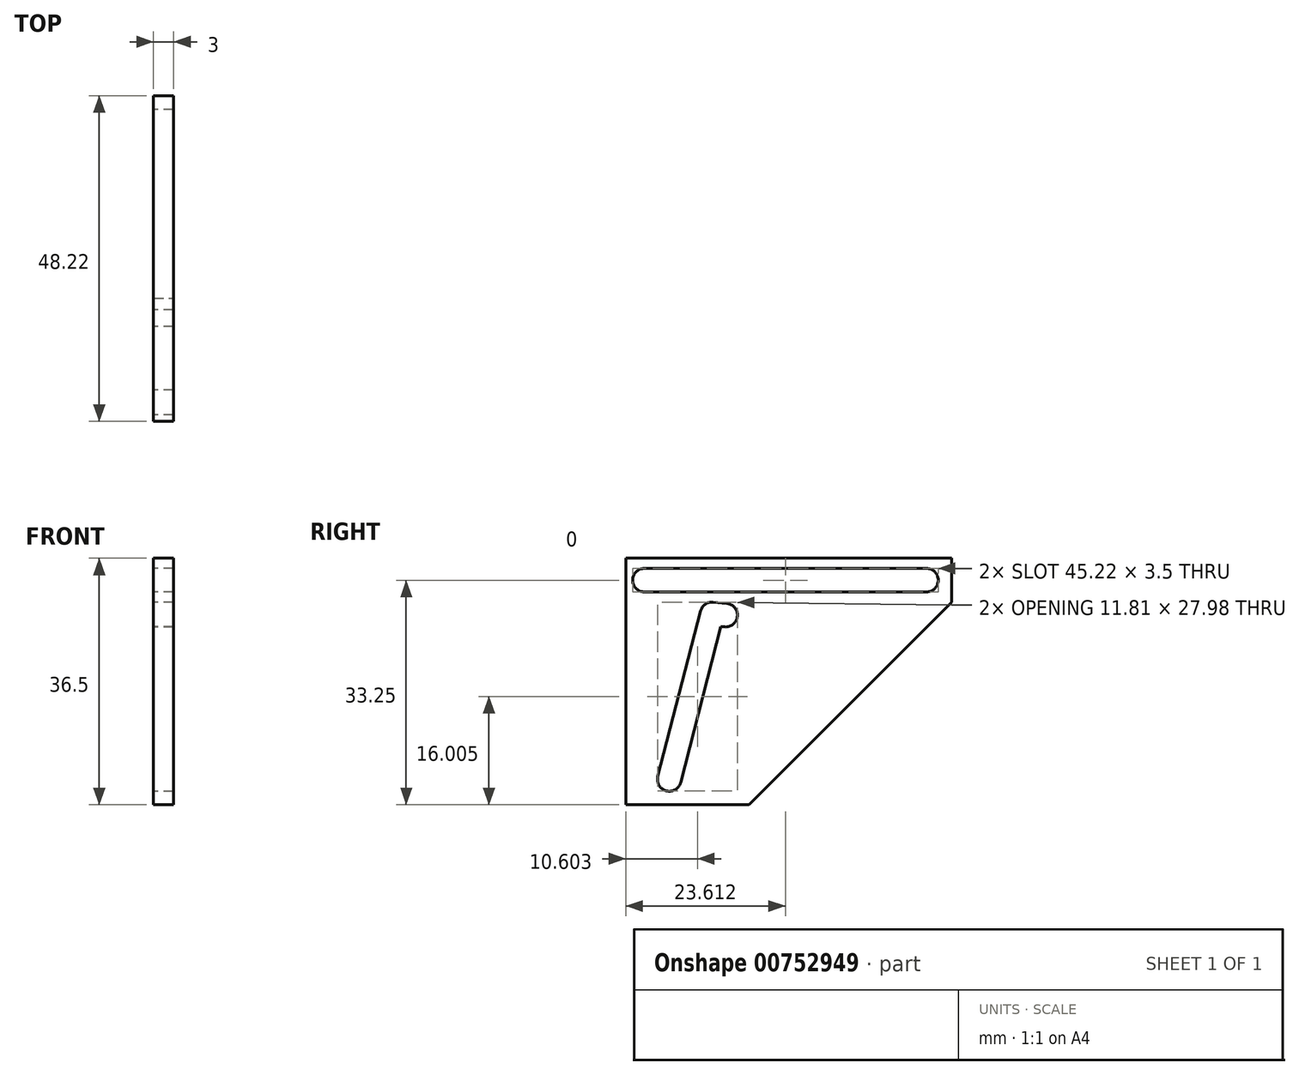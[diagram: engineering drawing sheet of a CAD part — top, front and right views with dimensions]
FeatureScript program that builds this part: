
annotation { "Feature Type Name" : "Feature", "Feature Type Description" : "" }
export const myFeature = defineFeature(function(context is Context, id is Id, definition is map)
    precondition{}
    {
        {
            var Q0;
            Q0=qCreatedBy(makeId("Right.planeOp"),FACE);
            var sketch = newSketch(context, id + "F0", { "sketchPlane" : qUnion([Q0])});
            skLineSegment(sketch, "E0", {"start": v(0, 29.5) * mm, "end": v(41.72, 29.5) * mm});
            skLineSegment(sketch, "E1", {"start": v(3.68, 0) * mm, "end": v(10, 24.5) * mm});
            skLineSegment(sketch, "E2.bottom", {"start": v(-2.75, 32.75) * mm, "end": v(45.47, 32.75) * mm});
            skLineSegment(sketch, "E2.top", {"start": v(-2.75, -3.75) * mm, "end": v(45.47, -3.75) * mm});
            skLineSegment(sketch, "E2.left", {"start": v(-2.75, 32.75) * mm, "end": v(-2.75, -3.75) * mm});
            skLineSegment(sketch, "E2.right", {"start": v(45.47, 32.75) * mm, "end": v(45.47, -3.75) * mm});
            skArc(sketch, "E3.0.startCap", {"start": v(0, 27.75) * mm, "mid": v(-1.75, 29.5) * mm, "end": v(0, 31.25) * mm});
            skArc(sketch, "E3.0.endCap", {"start": v(41.72, 31.25) * mm, "mid": v(43.47, 29.5) * mm, "end": v(41.72, 27.75) * mm});
            skLineSegment(sketch, "E3.0.left", {"start": v(0, 31.25) * mm, "end": v(41.72, 31.25) * mm});
            skLineSegment(sketch, "E3.0.right", {"start": v(0, 27.75) * mm, "end": v(41.72, 27.75) * mm});
            skArc(sketch, "E3.1.startCap", {"start": v(5.38, -0.44) * mm, "mid": v(3.24, -1.7) * mm, "end": v(1.99, 0.44) * mm});
            skArc(sketch, "E3.1.endCap", {"start": v(8.3, 24.94) * mm, "mid": v(10.44, 26.2) * mm, "end": v(11.7, 24.06) * mm});
            skLineSegment(sketch, "E3.1.left", {"start": v(1.99, 0.44) * mm, "end": v(8.3, 24.94) * mm});
            skLineSegment(sketch, "E3.1.right", {"start": v(5.38, -0.44) * mm, "end": v(11.7, 24.06) * mm});
            skLineSegment(sketch, "E4", {"start": v(10, 24.5) * mm, "end": v(12.01, 24.32) * mm});
            skArc(sketch, "E5.0.startCap", {"start": v(9.85, 22.76) * mm, "mid": v(8.26, 24.65) * mm, "end": v(10.15, 26.24) * mm});
            skArc(sketch, "E5.0.endCap", {"start": v(12.17, 26.07) * mm, "mid": v(13.76, 24.17) * mm, "end": v(11.86, 22.58) * mm});
            skLineSegment(sketch, "E5.0.left", {"start": v(10.15, 26.24) * mm, "end": v(12.17, 26.07) * mm});
            skLineSegment(sketch, "E5.0.right", {"start": v(9.85, 22.76) * mm, "end": v(11.86, 22.58) * mm});
            skSolve(sketch);
        }
        {
            var Q0;
            Q0=makeQuery(id+"F0.imprint","IMPRINT",FACE,{"disambiguationData":[TD([[makeQuery(id+"F0.imprint","IMPRINT",EDGE,{"derivedFrom":sQuery(id+"F0.wireOp",EDGE,"E2.bottom")}),-1.0]])]});
            extrude(context, id + "F1", {"entities" : qUnion([Q0]), "depth" : 3 * mm, "offsetDistance" : 25 * mm});
        }
        {
            var Q0;
            Q0=makeQuery(id+"F1.opExtrude","SWEPT_EDGE",EDGE,{"disambiguationData":[OSD([sQuery(id+"F0.wireOp",EDGE,"E2.top"),sQuery(id+"F0.wireOp",EDGE,"E2.right")])]});
            chamfer(context, id + "F2", {"entities" : qUnion([Q0]), "width" : 30 * mm, "tangentPropagation" : true});
        }
    });
